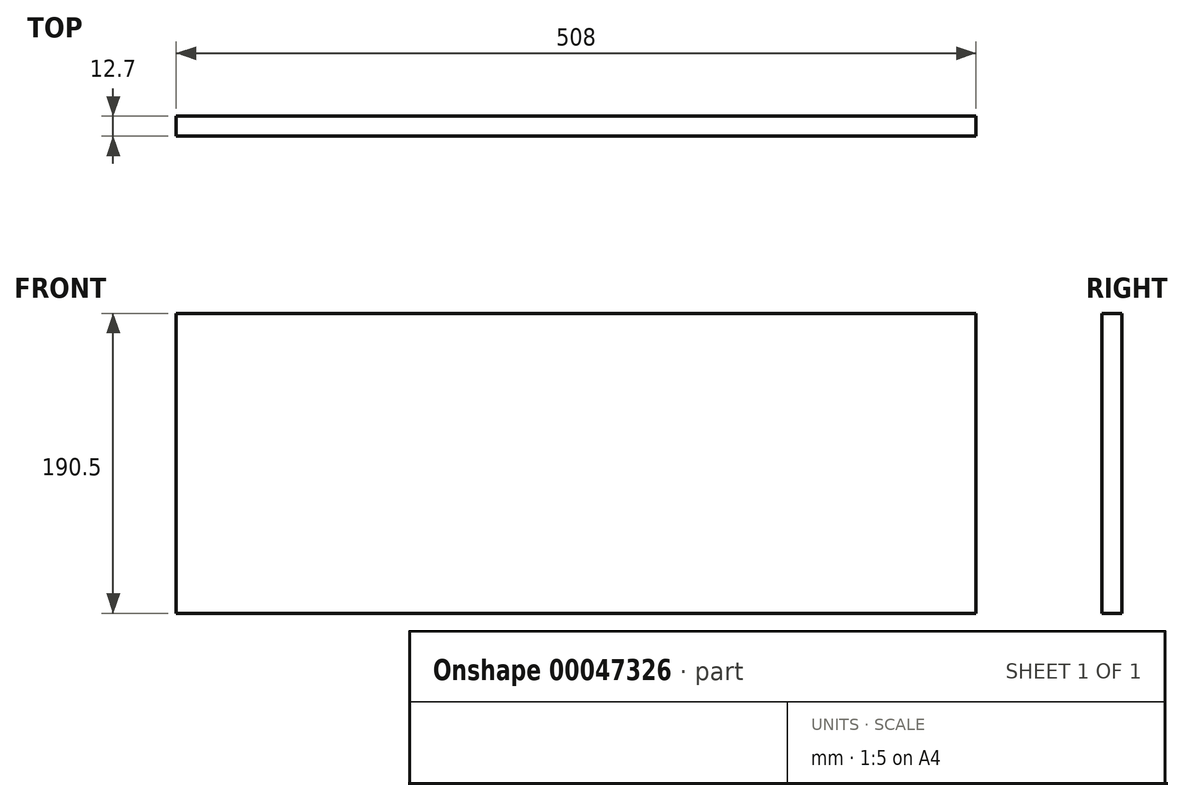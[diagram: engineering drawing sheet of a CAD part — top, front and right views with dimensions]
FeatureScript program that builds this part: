
annotation { "Feature Type Name" : "Feature", "Feature Type Description" : "" }
export const myFeature = defineFeature(function(context is Context, id is Id, definition is map)
    precondition{}
    {
        {
            var Q0;
            Q0=qCreatedBy(makeId("Front.planeOp"),FACE);
            var sketch = newSketch(context, id + "F0", { "sketchPlane" : qUnion([Q0])});
            skLineSegment(sketch, "E0.bottom", {"start": v(-48.44, 170.24) * mm, "end": v(459.56, 170.24) * mm});
            skLineSegment(sketch, "E0.top", {"start": v(-48.44, -20.26) * mm, "end": v(459.56, -20.26) * mm});
            skLineSegment(sketch, "E0.left", {"start": v(-48.44, 170.24) * mm, "end": v(-48.44, -20.26) * mm});
            skLineSegment(sketch, "E0.right", {"start": v(459.56, 170.24) * mm, "end": v(459.56, -20.26) * mm});
            skSolve(sketch);
        }
        {
            var Q0;
            Q0=makeQuery(id+"F0.imprint","IMPRINT",FACE,{"disambiguationData":[TD([[makeQuery(id+"F0.imprint","IMPRINT",EDGE,{"derivedFrom":sQuery(id+"F0.wireOp",EDGE,"E0.bottom")}),-1.0]])]});
            extrude(context, id + "F1", {"entities" : qUnion([Q0]), "depth" : 12.7 * mm});
        }
    });
